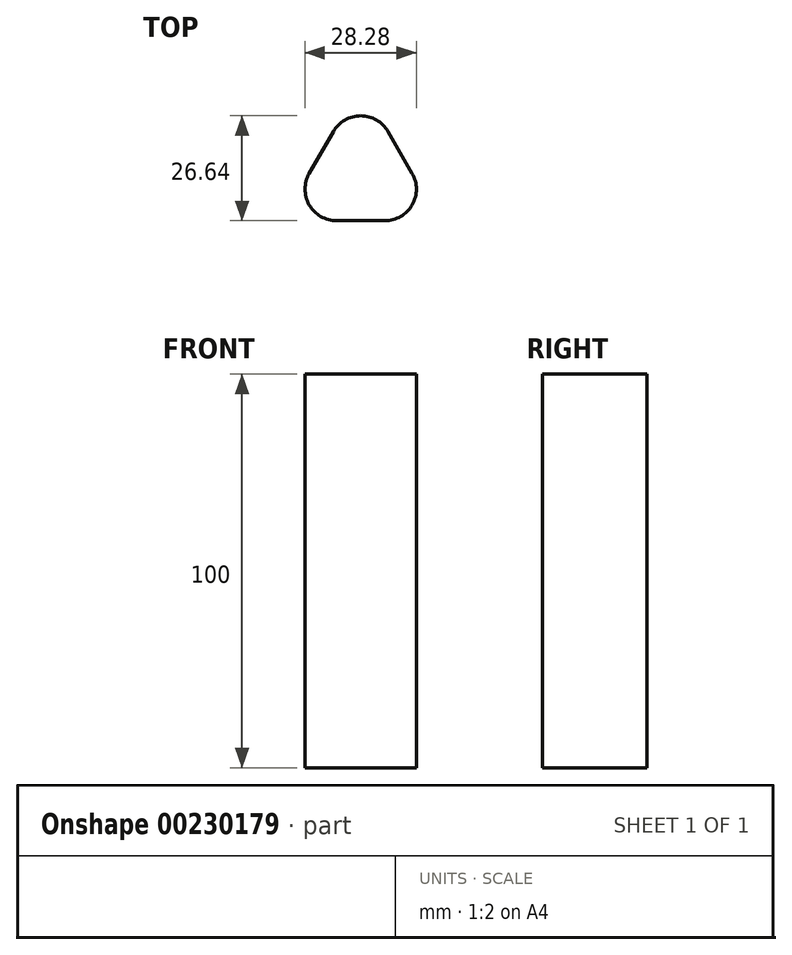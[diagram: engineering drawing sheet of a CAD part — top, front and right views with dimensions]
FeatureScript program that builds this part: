
annotation { "Feature Type Name" : "Feature", "Feature Type Description" : "" }
export const myFeature = defineFeature(function(context is Context, id is Id, definition is map)
    precondition{}
    {
        {
            var Q0;
            Q0=qCreatedBy(makeId("Top.planeOp"),FACE);
            var sketch = newSketch(context, id + "F0", { "sketchPlane" : qUnion([Q0])});
            skLineSegment(sketch, "E0", {"start": v(0, 0) * mm, "end": v(6.14, 0) * mm});
            skLineSegment(sketch, "E1", {"start": v(13.07, 12) * mm, "end": v(6.93, 22.64) * mm});
            skLineSegment(sketch, "E2", {"start": v(-6.93, 22.64) * mm, "end": v(-13.07, 12) * mm});
            skLineSegment(sketch, "E3", {"start": v(-6.14, 0) * mm, "end": v(0, 0) * mm});
            skPoint(sketch, "E4.visualSharp", {"position": v(0, 34.64) * mm});
            skArc(sketch, "E4.filletArc", {"start": v(6.93, 22.64) * mm, "mid": v(0, 26.64) * mm, "end": v(-6.93, 22.64) * mm});
            skPoint(sketch, "E5.visualSharp", {"position": v(-20, 0) * mm});
            skArc(sketch, "E5.filletArc", {"start": v(-13.07, 12) * mm, "mid": v(-13.07, 4) * mm, "end": v(-6.14, 0) * mm});
            skPoint(sketch, "E6.visualSharp", {"position": v(20, 0) * mm});
            skArc(sketch, "E6.filletArc", {"start": v(6.14, 0) * mm, "mid": v(13.07, 4) * mm, "end": v(13.07, 12) * mm});
            skSolve(sketch);
        }
        {
            var Q0;
            Q0 = qSketchRegion(id + "F0", true);
            extrude(context, id + "F1", {"entities" : qUnion([Q0]), "depth" : 100 * mm});
        }
    });
